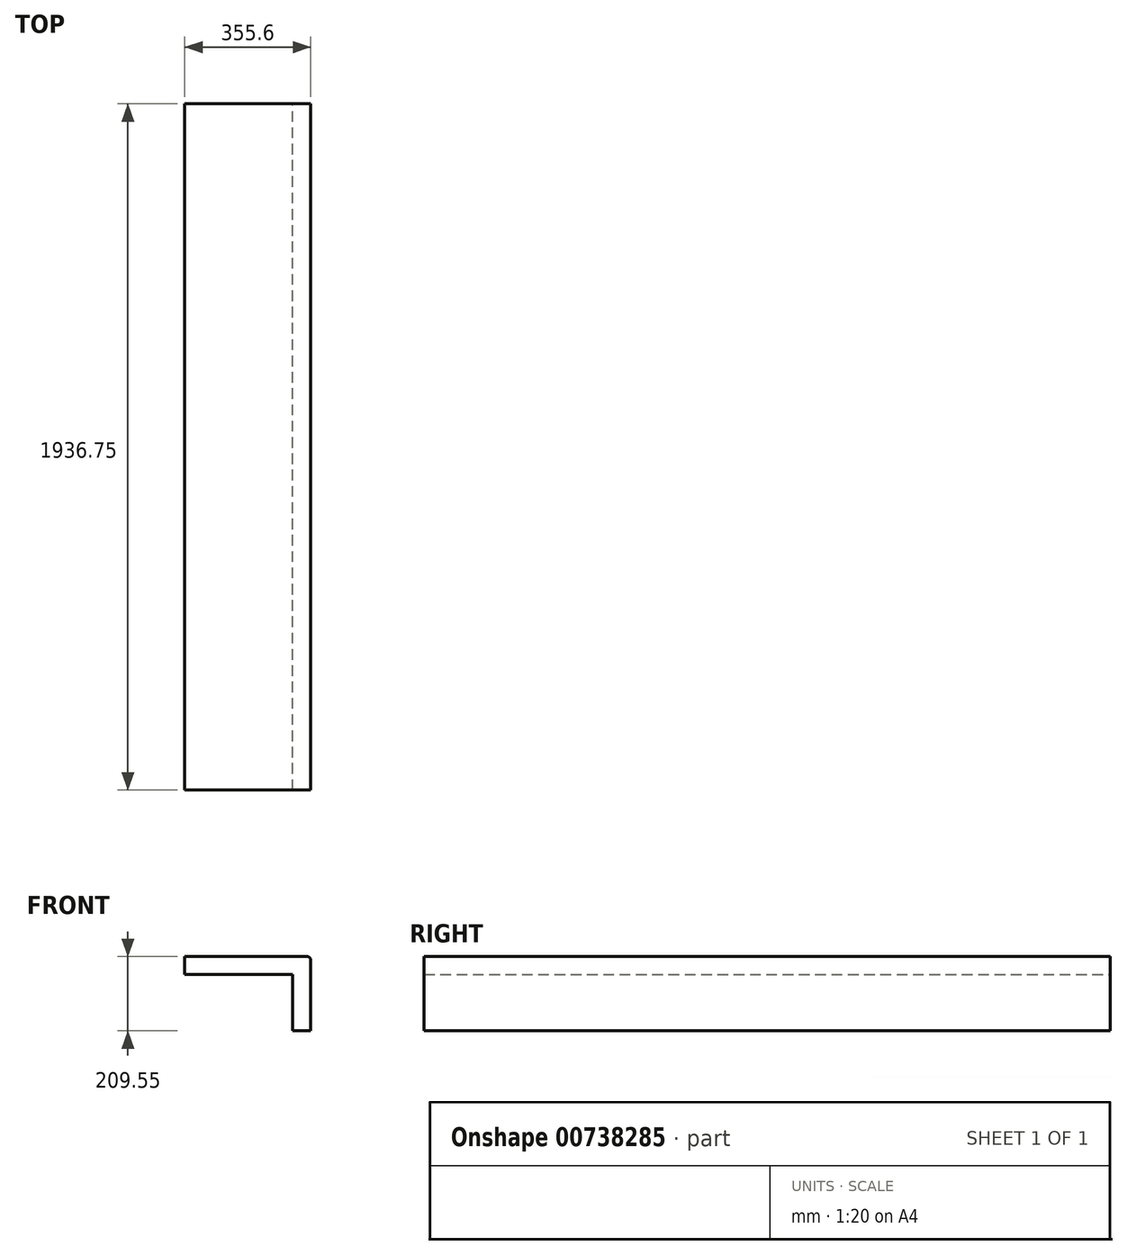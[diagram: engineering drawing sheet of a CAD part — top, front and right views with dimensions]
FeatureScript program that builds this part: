
annotation { "Feature Type Name" : "Feature", "Feature Type Description" : "" }
export const myFeature = defineFeature(function(context is Context, id is Id, definition is map)
    precondition{}
    {
        {
            var Q0;
            Q0=qCreatedBy(makeId("Front.planeOp"),FACE);
            var sketch = newSketch(context, id + "F0", { "sketchPlane" : qUnion([Q0])});
            skLineSegment(sketch, "E0", {"start": v(-147.5, 209.55) * mm, "end": v(-147.5, 158.75) * mm});
            skLineSegment(sketch, "E1", {"start": v(-147.5, 158.75) * mm, "end": v(157.3, 158.75) * mm});
            skLineSegment(sketch, "E2", {"start": v(157.3, 158.75) * mm, "end": v(157.3, 0) * mm});
            skLineSegment(sketch, "E3", {"start": v(208.1, 0) * mm, "end": v(157.3, 0) * mm});
            skLineSegment(sketch, "E4", {"start": v(-147.5, 209.55) * mm, "end": v(198.58, 209.55) * mm});
            skLineSegment(sketch, "E5", {"start": v(208.1, 200.03) * mm, "end": v(208.1, 0) * mm});
            skPoint(sketch, "E6.visualSharp", {"position": v(208.1, 209.55) * mm});
            skArc(sketch, "E6.filletArc", {"start": v(208.1, 200.03) * mm, "mid": v(205.31, 206.76) * mm, "end": v(198.58, 209.55) * mm});
            skSolve(sketch);
        }
        {
            var Q0;
            Q0=makeQuery(id+"F0.imprint","IMPRINT",FACE,{"disambiguationData":[TD([[makeQuery(id+"F0.imprint","IMPRINT",EDGE,{"derivedFrom":sQuery(id+"F0.wireOp",EDGE,"E0")}),1.0]])]});
            extrude(context, id + "F1", {"entities" : qUnion([Q0]), "depth" : 1936.75 * mm, "offsetDistance" : 25.4 * mm});
        }
    });
